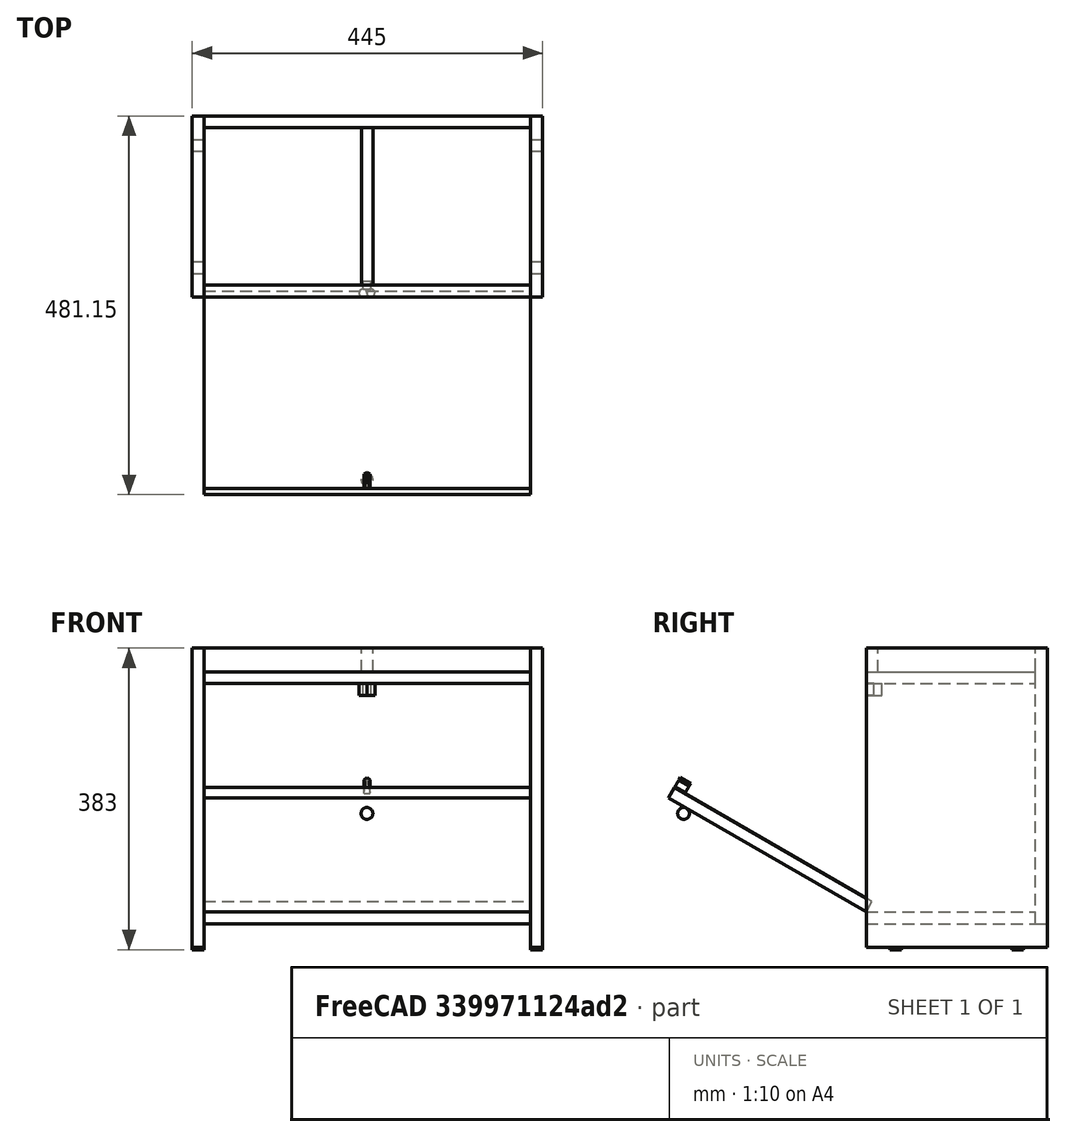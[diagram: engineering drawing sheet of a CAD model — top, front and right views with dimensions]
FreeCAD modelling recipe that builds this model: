
FCSTD DOCUMENT  (FreeCAD 0.17R13522 (Git))
Label: SuporteParaComedouroTamanho2
License: All rights reserved
LicenseURL: http://en.wikipedia.org/wiki/All_rights_reserved
objects: Part::Box×14, Part::Cylinder×4, Part::Cut×2, Part::Sphere×1, Part::MultiFuse×1, Part::Chamfer×1
note: 23 computed .brp shape members not serialized (recipe doc carries the construction recipe); baked Part::Feature solids carry a one-line shape summary decoded from their .brp

FEATURE [Part::Box] Box  label="SuporteFrenteSuperiorVertical"
  AttacherType = Attacher::AttachEngine3D
  Height = 30
  Length = 415
  Width = 15
FEATURE [Part::Box] Box001  label="SuporteLateralVerticalEsquerdo"
  AttacherType = Attacher::AttachEngine3D
  Height = 380
  Length = 15
  Placement = pos=(-15,0,-350) rot=(0,0,1;0rad)
  Width = 230
FEATURE [Part::Box] Box002  label="SuporteLateralVerticalDireito"
  AttacherType = Attacher::AttachEngine3D
  Height = 380
  Length = 15
  Placement = pos=(415,0,-350) rot=(0,0,1;0rad)
  Width = 230
FEATURE [Part::Box] Box003  label="TampoSuperiorHorizontal"
  AttacherType = Attacher::AttachEngine3D
  Height = 15
  Length = 415
  Placement = pos=(0,0,-15) rot=(0,0,1;0rad)
  Width = 215
FEATURE [Part::Box] Box004  label="SuporteFundoVertical"
  AttacherType = Attacher::AttachEngine3D
  Height = 350
  Length = 415
  Placement = pos=(0,215,-320) rot=(0,0,1;0rad)
  Width = 15
FEATURE [Part::Box] Box005  label="SuporteVerticalMeio"
  AttacherType = Attacher::AttachEngine3D
  Height = 30
  Length = 15
  Placement = pos=(200,15,0) rot=(0,0,1;0rad)
  Width = 200
FEATURE [Part::Box] Box006  label="TampoInferiorHorizontal"
  AttacherType = Attacher::AttachEngine3D
  Height = 15
  Length = 415
  Placement = pos=(0,0,-320) rot=(0,0,1;0rad)
  Width = 215
FEATURE [Part::Box] Box007  label="Cube"
  AttacherType = Attacher::AttachEngine3D
  Height = 3
  Length = 15
  Placement = pos=(-15,30,-353) rot=(0,0,1;0rad)
  Width = 15
FEATURE [Part::Box] Box008  label="Cube001"
  AttacherType = Attacher::AttachEngine3D
  Height = 3
  Length = 15
  Placement = pos=(-15,185,-353) rot=(0,0,1;0rad)
  Width = 15
FEATURE [Part::Box] Box009  label="Cube002"
  AttacherType = Attacher::AttachEngine3D
  Height = 3
  Length = 15
  Placement = pos=(415,30,-353) rot=(0,0,1;0rad)
  Width = 15
FEATURE [Part::Box] Box010  label="Cube003"
  AttacherType = Attacher::AttachEngine3D
  Height = 3
  Length = 15
  Placement = pos=(415,185,-353) rot=(0,0,1;0rad)
  Width = 15
FEATURE [Part::Box] Box011  label="TampaBasculante"
  AttacherType = Attacher::AttachEngine3D
  Height = 290
  Length = 415
  Placement = pos=(0,0,-305) rot=(1,0,0;1.0472rad)
  Width = 15
FEATURE [Part::Sphere] Sphere  label="Puxador"
  Angle1 = -90
  Angle2 = 90
  Angle3 = 360
  AttacherType = Attacher::AttachEngine3D
  Placement = pos=(207,-232,-180) rot=(0,0,1;0rad)
  Radius = 7.5
FEATURE [Part::Cylinder] Cylinder
  Angle = 360
  AttacherType = Attacher::AttachEngine3D
  Height = 15
  Placement = pos=(-100,0,0) rot=(0,0,1;0rad)
  Radius = 5
FEATURE [Part::Cylinder] Cylinder001
  Angle = 360
  AttacherType = Attacher::AttachEngine3D
  Height = 15
  Placement = pos=(-90,0,0) rot=(0,0,1;0rad)
  Radius = 5
FEATURE [Part::Box] Box012  label="Cube004"
  AttacherType = Attacher::AttachEngine3D
  Height = 15
  Length = 10
  Placement = pos=(-100,5,0) rot=(0,0,1;0rad)
  Width = 10
FEATURE [Part::MultiFuse] Fusion
  Placement = pos=(302,5,-30) rot=(0,0,1;0rad)
  Shapes = -> [Cylinder,Cylinder001,Box012]
FEATURE [Part::Box] Box013  label="Cube005"
  AttacherType = Attacher::AttachEngine3D
  Height = 15
  Length = 8
  Placement = pos=(193,-130,-70) rot=(0,0,1;0rad)
  Width = 15
FEATURE [Part::Chamfer] Chamfer
  Base = -> Box013
  Edges = 2 edges r=3.9: [Edge3,Edge7]
FEATURE [Part::Cylinder] Cylinder002
  Angle = 360
  AttacherType = Attacher::AttachEngine3D
  Height = 15
  Placement = pos=(212,-124,-70) rot=(0,0,1;0rad)
  Radius = 12
FEATURE [Part::Cylinder] Cylinder003
  Angle = 360
  AttacherType = Attacher::AttachEngine3D
  Height = 15
  Placement = pos=(182,-124,-70) rot=(0,0,1;0rad)
  Radius = 12
FEATURE [Part::Cut] Cut
  Base = -> Chamfer
  Tool = -> Cylinder002
FEATURE [Part::Cut] Cut001
  Base = -> Cut
  Placement = pos=(10,-226,-7) rot=(1,0,0;1.0472rad)
  Tool = -> Cylinder003
